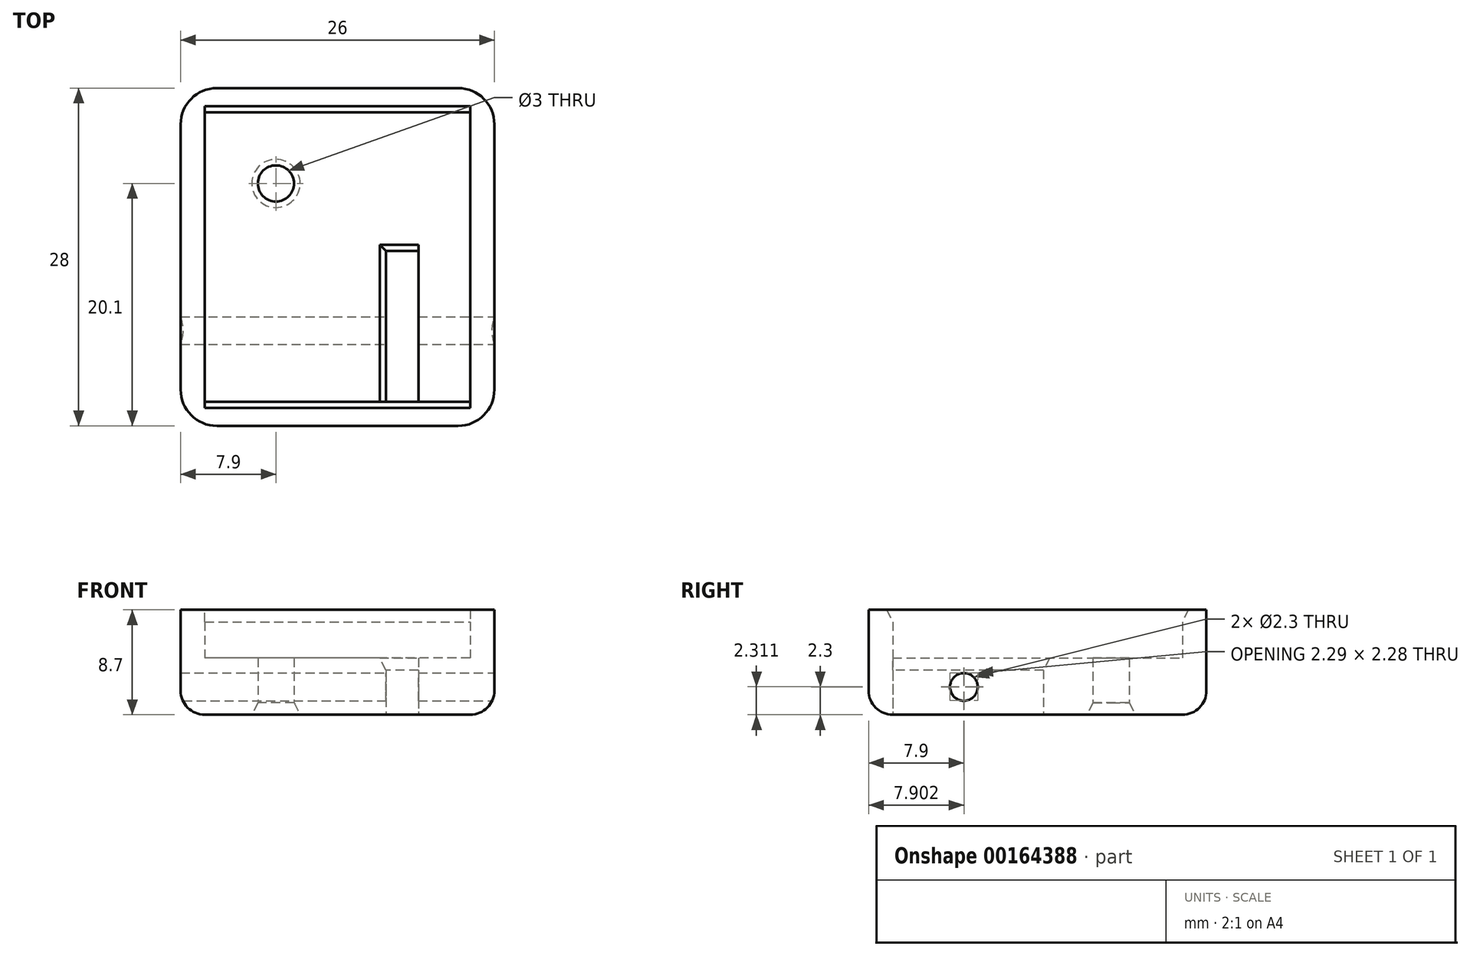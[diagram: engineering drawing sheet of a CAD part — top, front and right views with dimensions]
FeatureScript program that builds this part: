
annotation { "Feature Type Name" : "Feature", "Feature Type Description" : "" }
export const myFeature = defineFeature(function(context is Context, id is Id, definition is map)
    precondition{}
    {
        {
            var Q0;
            Q0=qCreatedBy(makeId("Top.planeOp"),FACE);
            var sketch = newSketch(context, id + "F0", { "sketchPlane" : qUnion([Q0])});
            skLineSegment(sketch, "E0.bottom", {"start": v(-11, 11.5) * mm, "end": v(11, 11.5) * mm});
            skLineSegment(sketch, "E0.top", {"start": v(-11, -12.5) * mm, "end": v(11, -12.5) * mm});
            skLineSegment(sketch, "E0.left", {"start": v(-11, 11.5) * mm, "end": v(-11, -12.5) * mm});
            skLineSegment(sketch, "E0.right", {"start": v(11, 11.5) * mm, "end": v(11, -12.5) * mm});
            skLineSegment(sketch, "E1.top", {"start": v(-11, 13.5) * mm, "end": v(11, 13.5) * mm});
            skLineSegment(sketch, "E1.left", {"start": v(-11, 11.5) * mm, "end": v(-11, 13.5) * mm});
            skLineSegment(sketch, "E1.right", {"start": v(11, 11.5) * mm, "end": v(11, 13.5) * mm});
            skLineSegment(sketch, "E2.top", {"start": v(-11, -14.5) * mm, "end": v(11, -14.5) * mm});
            skLineSegment(sketch, "E2.left", {"start": v(-11, -12.5) * mm, "end": v(-11, -14.5) * mm});
            skLineSegment(sketch, "E2.right", {"start": v(11, -12.5) * mm, "end": v(11, -14.5) * mm});
            skLineSegment(sketch, "E3.bottom", {"start": v(-11, 13.5) * mm, "end": v(-13, 13.5) * mm});
            skLineSegment(sketch, "E3.top", {"start": v(-11, -14.5) * mm, "end": v(-13, -14.5) * mm});
            skLineSegment(sketch, "E3.left", {"start": v(-11, 13.5) * mm, "end": v(-11, -14.5) * mm});
            skLineSegment(sketch, "E3.right", {"start": v(-13, 13.5) * mm, "end": v(-13, -14.5) * mm});
            skLineSegment(sketch, "E4.bottom", {"start": v(11, 13.5) * mm, "end": v(13, 13.5) * mm});
            skLineSegment(sketch, "E4.top", {"start": v(11, -14.5) * mm, "end": v(13, -14.5) * mm});
            skLineSegment(sketch, "E4.left", {"start": v(11, 13.5) * mm, "end": v(11, -14.5) * mm});
            skLineSegment(sketch, "E4.right", {"start": v(13, 13.5) * mm, "end": v(13, -14.5) * mm});
            skCircle(sketch, "E5", {"center": v(-5.1, 5.6) * mm, "radius": 1.5 * mm});
            skLineSegment(sketch, "E6.bottom", {"start": v(4, -12.5) * mm, "end": v(6.7, -12.5) * mm});
            skLineSegment(sketch, "E6.top", {"start": v(4, 0) * mm, "end": v(6.7, 0) * mm});
            skLineSegment(sketch, "E6.left", {"start": v(4, -12.5) * mm, "end": v(4, 0) * mm});
            skLineSegment(sketch, "E6.right", {"start": v(6.7, -12.5) * mm, "end": v(6.7, 0) * mm});
            skSolve(sketch);
        }
        {
            var Q0;
            Q0 = qSketchRegion(id + "F0", true);
            var Q1;
            {var subQ3=sQuery(id+"F0.wireOp",EDGE,"E0.top");Q1=makeQuery(id+"F0.imprint","IMPRINT",FACE,{"disambiguationData":[TD([[makeQuery(id+"F0.imprint","IMPRINT",EDGE,{"derivedFrom":subQ3}),1.0]])]});}
            var Q2;
            Q2=makeQuery(id+"F0.imprint","IMPRINT",FACE,{"disambiguationData":[TD([[makeQuery(id+"F0.imprint","IMPRINT",EDGE,{"derivedFrom":sQuery(id+"F0.wireOp",EDGE,"E5")}),-1.0]])]});
            var Q3;
            {var subQ0=sQuery(id+"F0.wireOp",EDGE,"E3.left");var subQ1=sQuery(id+"F0.wireOp",EDGE,"E0.bottom");var subQ2=makeQuery(id+"F0.imprint","INTERSECT",VERTEX,{"derivedFrom":[subQ1,subQ0]});Q3=makeQuery(id+"F0.imprint","IMPRINT",FACE,{"disambiguationData":[TD([[makeQuery(id+"F0.imprint","IMPRINT",EDGE,{"disambiguationData":[TD([[subQ2,-1.0]])],"derivedFrom":subQ1}),-1.0]])]});}
            extrude(context, id + "F1", {"entities" : qUnion([Q0, Q1, Q2, Q3]), "depth" : 4.7 * mm});
        }
        {
            var Q0;
            {var subQ3=sQuery(id+"F0.wireOp",EDGE,"E4.bottom");Q0=makeQuery(id+"F0.imprint","IMPRINT",FACE,{"disambiguationData":[TD([[makeQuery(id+"F0.imprint","IMPRINT",EDGE,{"derivedFrom":subQ3}),-1.0]])]});}
            var Q1;
            {var subQ0=sQuery(id+"F0.wireOp",EDGE,"E0.top");Q1=makeQuery(id+"F0.imprint","IMPRINT",FACE,{"disambiguationData":[TD([[makeQuery(id+"F0.imprint","IMPRINT",EDGE,{"derivedFrom":subQ0}),-1.0]])]});}
            var Q2;
            {var subQ3=sQuery(id+"F0.wireOp",EDGE,"E3.bottom");Q2=makeQuery(id+"F0.imprint","IMPRINT",FACE,{"disambiguationData":[TD([[makeQuery(id+"F0.imprint","IMPRINT",EDGE,{"derivedFrom":subQ3}),1.0]])]});}
            var Q3;
            {var subQ3=sQuery(id+"F0.wireOp",EDGE,"E1.top");Q3=makeQuery(id+"F0.imprint","IMPRINT",FACE,{"disambiguationData":[TD([[makeQuery(id+"F0.imprint","IMPRINT",EDGE,{"derivedFrom":subQ3}),-1.0]])]});}
            extrude(context, id + "F2", {"entities" : qUnion([Q0, Q1, Q2, Q3]), "operationType" : NewBodyOperationType.ADD, "depth" : 8.7 * mm});
        }
        {
            var Q0;
            Q0=makeQuery(id+"F1.opExtrude","CAP_FACE",FACE,{"disambiguationData":[OSD([sQuery(id+"F0.wireOp",EDGE,"E1.top"),sQuery(id+"F0.wireOp",EDGE,"E2.top"),sQuery(id+"F0.wireOp",EDGE,"E3.bottom"),sQuery(id+"F0.wireOp",EDGE,"E3.top"),sQuery(id+"F0.wireOp",EDGE,"E3.right"),sQuery(id+"F0.wireOp",EDGE,"E4.bottom"),sQuery(id+"F0.wireOp",EDGE,"E4.top"),sQuery(id+"F0.wireOp",EDGE,"E4.right")])],"isStart":false});
            var sketch = newSketch(context, id + "F3", { "sketchPlane" : qUnion([Q0])});
            skCircle(sketch, "E7", {"center": v(-5.1, 5.6) * mm, "radius": 1.5 * mm});
            skSolve(sketch);
        }
        {
            var Q0;
            Q0 = qSketchRegion(id + "F3", true);
            extrude(context, id + "F4", {"entities" : qUnion([Q0]), "operationType" : NewBodyOperationType.REMOVE, "endBound" : BoundingType.THROUGH_ALL, "oppositeDirection" : true, "depth" : 25 * mm});
        }
        {
            var Q0;
            {var subQ0=sQuery(id+"F0.wireOp",EDGE,"E4.right");Q0=makeQuery(id+"F2.boolean.opBoolean","MERGE",FACE,{"derivedFrom":[makeQuery(id+"F1.opExtrude","SWEPT_FACE",FACE,{"disambiguationData":[OSD([subQ0])]}),makeQuery(id+"F2.opExtrude","SWEPT_FACE",FACE,{"disambiguationData":[OSD([subQ0])]})]});}
            var sketch = newSketch(context, id + "F5", { "sketchPlane" : qUnion([Q0])});
            skCircle(sketch, "E8", {"center": v(-6.6, 2.3) * mm, "radius": 1.15 * mm});
            skSolve(sketch);
        }
        {
            var Q0;
            Q0=makeQuery(id+"F2.opExtrude","CAP_EDGE",EDGE,{"disambiguationData":[OSD([sQuery(id+"F0.wireOp",EDGE,"E0.bottom")])],"isStart":false});
            var Q1;
            Q1=makeQuery(id+"F2.opExtrude","CAP_EDGE",EDGE,{"disambiguationData":[OSD([sQuery(id+"F0.wireOp",EDGE,"E4.left")])],"isStart":false});
            var Q2;
            Q2=makeQuery(id+"F2.opExtrude","CAP_EDGE",EDGE,{"disambiguationData":[OSD([sQuery(id+"F0.wireOp",EDGE,"E3.left")])],"isStart":false});
            var Q3;
            Q3=makeQuery(id+"F2.opExtrude","CAP_EDGE",EDGE,{"disambiguationData":[OSD([sQuery(id+"F0.wireOp",EDGE,"E0.top"),sQuery(id+"F0.wireOp",EDGE,"E6.bottom")])],"isStart":false});
            var Q4;
            Q4=makeQuery(id+"F1.opExtrude","CAP_EDGE",EDGE,{"disambiguationData":[OSD([sQuery(id+"F0.wireOp",EDGE,"E5")])],"isStart":true});
            var Q5;
            Q5=makeQuery(id+"F1.opExtrude","CAP_EDGE",EDGE,{"disambiguationData":[OSD([sQuery(id+"F0.wireOp",EDGE,"E6.top")])],"isStart":false});
            var Q6;
            Q6=makeQuery(id+"F1.opExtrude","CAP_EDGE",EDGE,{"disambiguationData":[OSD([sQuery(id+"F0.wireOp",EDGE,"E6.left")])],"isStart":false});
            chamfer(context, id + "F6", {"entities" : qUnion([Q0, Q1, Q2, Q3, Q4, Q5, Q6]), "chamferType" : ChamferType.TWO_OFFSETS, "width1" : 0.5 * mm, "oppositeDirection" : false, "width2" : 1 * mm, "tangentPropagation" : true});
        }
        {
            var Q0;
            {var subQ0=sQuery(id+"F0.wireOp",EDGE,"E3.right");var subQ1=sQuery(id+"F0.wireOp",EDGE,"E3.top");Q0=makeQuery(id+"F2.boolean.opBoolean","MERGE",EDGE,{"derivedFrom":[makeQuery(id+"F1.opExtrude","SWEPT_EDGE",EDGE,{"disambiguationData":[OSD([subQ1,subQ0])]}),makeQuery(id+"F2.opExtrude","SWEPT_EDGE",EDGE,{"disambiguationData":[OSD([subQ1,subQ0])]})]});}
            var Q1;
            {var subQ0=sQuery(id+"F0.wireOp",EDGE,"E4.right");var subQ1=sQuery(id+"F0.wireOp",EDGE,"E4.top");Q1=makeQuery(id+"F2.boolean.opBoolean","MERGE",EDGE,{"derivedFrom":[makeQuery(id+"F1.opExtrude","SWEPT_EDGE",EDGE,{"disambiguationData":[OSD([subQ1,subQ0])]}),makeQuery(id+"F2.opExtrude","SWEPT_EDGE",EDGE,{"disambiguationData":[OSD([subQ1,subQ0])]})]});}
            var Q2;
            {var subQ0=sQuery(id+"F0.wireOp",EDGE,"E3.right");var subQ1=sQuery(id+"F0.wireOp",EDGE,"E3.bottom");Q2=makeQuery(id+"F2.boolean.opBoolean","MERGE",EDGE,{"derivedFrom":[makeQuery(id+"F1.opExtrude","SWEPT_EDGE",EDGE,{"disambiguationData":[OSD([subQ1,subQ0])]}),makeQuery(id+"F2.opExtrude","SWEPT_EDGE",EDGE,{"disambiguationData":[OSD([subQ1,subQ0])]})]});}
            var Q3;
            {var subQ0=sQuery(id+"F0.wireOp",EDGE,"E4.right");var subQ1=sQuery(id+"F0.wireOp",EDGE,"E4.bottom");Q3=makeQuery(id+"F2.boolean.opBoolean","MERGE",EDGE,{"derivedFrom":[makeQuery(id+"F1.opExtrude","SWEPT_EDGE",EDGE,{"disambiguationData":[OSD([subQ1,subQ0])]}),makeQuery(id+"F2.opExtrude","SWEPT_EDGE",EDGE,{"disambiguationData":[OSD([subQ1,subQ0])]})]});}
            fillet(context, id + "F7", {"entities" : qUnion([Q0, Q1, Q2, Q3]), "radius" : 3 * mm, "tangentPropagation" : true, "allowEdgeOverflow" : false});
        }
        {
            var Q0;
            Q0=makeQuery(id+"F1.opExtrude","CAP_EDGE",EDGE,{"disambiguationData":[OSD([sQuery(id+"F0.wireOp",EDGE,"E4.right")])],"isStart":true});
            var Q1;
            {var subQ0=sQuery(id+"F0.wireOp",EDGE,"E4.right");var subQ1=sQuery(id+"F0.wireOp",EDGE,"E4.top");Q1=makeQuery(id+"F7.opFillet","BLEND_EDGE",EDGE,{"blendedFrom":[makeQuery(id+"F2.boolean.opBoolean","MERGE",EDGE,{"derivedFrom":[makeQuery(id+"F1.opExtrude","SWEPT_EDGE",EDGE,{"disambiguationData":[OSD([subQ1,subQ0])]}),makeQuery(id+"F2.opExtrude","SWEPT_EDGE",EDGE,{"disambiguationData":[OSD([subQ1,subQ0])]})]}),makeQuery(id+"F1.opExtrude","CAP_FACE",FACE,{"disambiguationData":[OSD([sQuery(id+"F0.wireOp",EDGE,"E1.top"),sQuery(id+"F0.wireOp",EDGE,"E2.top"),sQuery(id+"F0.wireOp",EDGE,"E3.bottom"),sQuery(id+"F0.wireOp",EDGE,"E3.top"),sQuery(id+"F0.wireOp",EDGE,"E3.right"),sQuery(id+"F0.wireOp",EDGE,"E4.bottom"),subQ1,subQ0,sQuery(id+"F0.wireOp",EDGE,"E5")])],"isStart":true})],"blendedInto":[makeQuery(id+"F1.opExtrude","CAP_FACE",FACE,{"disambiguationData":[OSD([sQuery(id+"F0.wireOp",EDGE,"E1.top"),sQuery(id+"F0.wireOp",EDGE,"E2.top"),sQuery(id+"F0.wireOp",EDGE,"E3.bottom"),sQuery(id+"F0.wireOp",EDGE,"E3.top"),sQuery(id+"F0.wireOp",EDGE,"E3.right"),sQuery(id+"F0.wireOp",EDGE,"E4.bottom"),subQ1,subQ0,sQuery(id+"F0.wireOp",EDGE,"E5")])],"isStart":true})]});}
            var Q2;
            Q2=makeQuery(id+"F1.opExtrude","CAP_EDGE",EDGE,{"disambiguationData":[OSD([sQuery(id+"F0.wireOp",EDGE,"E2.top"),sQuery(id+"F0.wireOp",EDGE,"E3.top"),sQuery(id+"F0.wireOp",EDGE,"E4.top")])],"isStart":true});
            var Q3;
            {var subQ0=sQuery(id+"F0.wireOp",EDGE,"E3.right");var subQ1=sQuery(id+"F0.wireOp",EDGE,"E3.top");Q3=makeQuery(id+"F7.opFillet","BLEND_EDGE",EDGE,{"blendedFrom":[makeQuery(id+"F2.boolean.opBoolean","MERGE",EDGE,{"derivedFrom":[makeQuery(id+"F1.opExtrude","SWEPT_EDGE",EDGE,{"disambiguationData":[OSD([subQ1,subQ0])]}),makeQuery(id+"F2.opExtrude","SWEPT_EDGE",EDGE,{"disambiguationData":[OSD([subQ1,subQ0])]})]}),makeQuery(id+"F1.opExtrude","CAP_FACE",FACE,{"disambiguationData":[OSD([sQuery(id+"F0.wireOp",EDGE,"E1.top"),sQuery(id+"F0.wireOp",EDGE,"E2.top"),sQuery(id+"F0.wireOp",EDGE,"E3.bottom"),subQ1,subQ0,sQuery(id+"F0.wireOp",EDGE,"E4.bottom"),sQuery(id+"F0.wireOp",EDGE,"E4.top"),sQuery(id+"F0.wireOp",EDGE,"E4.right"),sQuery(id+"F0.wireOp",EDGE,"E5")])],"isStart":true})],"blendedInto":[makeQuery(id+"F1.opExtrude","CAP_FACE",FACE,{"disambiguationData":[OSD([sQuery(id+"F0.wireOp",EDGE,"E1.top"),sQuery(id+"F0.wireOp",EDGE,"E2.top"),sQuery(id+"F0.wireOp",EDGE,"E3.bottom"),subQ1,subQ0,sQuery(id+"F0.wireOp",EDGE,"E4.bottom"),sQuery(id+"F0.wireOp",EDGE,"E4.top"),sQuery(id+"F0.wireOp",EDGE,"E4.right"),sQuery(id+"F0.wireOp",EDGE,"E5")])],"isStart":true})]});}
            var Q4;
            {var subQ0=sQuery(id+"F0.wireOp",EDGE,"E4.right");var subQ1=sQuery(id+"F0.wireOp",EDGE,"E4.bottom");Q4=makeQuery(id+"F7.opFillet","BLEND_EDGE",EDGE,{"blendedFrom":[makeQuery(id+"F2.boolean.opBoolean","MERGE",EDGE,{"derivedFrom":[makeQuery(id+"F1.opExtrude","SWEPT_EDGE",EDGE,{"disambiguationData":[OSD([subQ1,subQ0])]}),makeQuery(id+"F2.opExtrude","SWEPT_EDGE",EDGE,{"disambiguationData":[OSD([subQ1,subQ0])]})]}),makeQuery(id+"F1.opExtrude","CAP_FACE",FACE,{"disambiguationData":[OSD([sQuery(id+"F0.wireOp",EDGE,"E1.top"),sQuery(id+"F0.wireOp",EDGE,"E2.top"),sQuery(id+"F0.wireOp",EDGE,"E3.bottom"),sQuery(id+"F0.wireOp",EDGE,"E3.top"),sQuery(id+"F0.wireOp",EDGE,"E3.right"),subQ1,sQuery(id+"F0.wireOp",EDGE,"E4.top"),subQ0,sQuery(id+"F0.wireOp",EDGE,"E5")])],"isStart":true})],"blendedInto":[makeQuery(id+"F1.opExtrude","CAP_FACE",FACE,{"disambiguationData":[OSD([sQuery(id+"F0.wireOp",EDGE,"E1.top"),sQuery(id+"F0.wireOp",EDGE,"E2.top"),sQuery(id+"F0.wireOp",EDGE,"E3.bottom"),sQuery(id+"F0.wireOp",EDGE,"E3.top"),sQuery(id+"F0.wireOp",EDGE,"E3.right"),subQ1,sQuery(id+"F0.wireOp",EDGE,"E4.top"),subQ0,sQuery(id+"F0.wireOp",EDGE,"E5")])],"isStart":true})]});}
            var Q5;
            Q5=makeQuery(id+"F1.opExtrude","CAP_EDGE",EDGE,{"disambiguationData":[OSD([sQuery(id+"F0.wireOp",EDGE,"E1.top"),sQuery(id+"F0.wireOp",EDGE,"E3.bottom"),sQuery(id+"F0.wireOp",EDGE,"E4.bottom")])],"isStart":true});
            var Q6;
            {var subQ0=sQuery(id+"F0.wireOp",EDGE,"E3.right");var subQ1=sQuery(id+"F0.wireOp",EDGE,"E3.bottom");Q6=makeQuery(id+"F7.opFillet","BLEND_EDGE",EDGE,{"blendedFrom":[makeQuery(id+"F2.boolean.opBoolean","MERGE",EDGE,{"derivedFrom":[makeQuery(id+"F1.opExtrude","SWEPT_EDGE",EDGE,{"disambiguationData":[OSD([subQ1,subQ0])]}),makeQuery(id+"F2.opExtrude","SWEPT_EDGE",EDGE,{"disambiguationData":[OSD([subQ1,subQ0])]})]}),makeQuery(id+"F1.opExtrude","CAP_FACE",FACE,{"disambiguationData":[OSD([sQuery(id+"F0.wireOp",EDGE,"E1.top"),sQuery(id+"F0.wireOp",EDGE,"E2.top"),subQ1,sQuery(id+"F0.wireOp",EDGE,"E3.top"),subQ0,sQuery(id+"F0.wireOp",EDGE,"E4.bottom"),sQuery(id+"F0.wireOp",EDGE,"E4.top"),sQuery(id+"F0.wireOp",EDGE,"E4.right"),sQuery(id+"F0.wireOp",EDGE,"E5")])],"isStart":true})],"blendedInto":[makeQuery(id+"F1.opExtrude","CAP_FACE",FACE,{"disambiguationData":[OSD([sQuery(id+"F0.wireOp",EDGE,"E1.top"),sQuery(id+"F0.wireOp",EDGE,"E2.top"),subQ1,sQuery(id+"F0.wireOp",EDGE,"E3.top"),subQ0,sQuery(id+"F0.wireOp",EDGE,"E4.bottom"),sQuery(id+"F0.wireOp",EDGE,"E4.top"),sQuery(id+"F0.wireOp",EDGE,"E4.right"),sQuery(id+"F0.wireOp",EDGE,"E5")])],"isStart":true})]});}
            var Q7;
            Q7=makeQuery(id+"F1.opExtrude","CAP_EDGE",EDGE,{"disambiguationData":[OSD([sQuery(id+"F0.wireOp",EDGE,"E3.right")])],"isStart":true});
            var Q8;
            Q8=makeQuery(id+"FJWYh7fez7YNRAC_1.opExtrude","CAP_EDGE",EDGE,{"disambiguationData":[OSD([sQuery(id+"F0.wireOp",EDGE,"lFoeRRYX-G3Lz-FDY6-PA7t-A0xL0vWlHZZd")])],"isStart":false});
            fillet(context, id + "F8", {"entities" : qUnion([Q0, Q1, Q2, Q3, Q4, Q5, Q6, Q7, Q8]), "radius" : 2 * mm, "tangentPropagation" : true, "allowEdgeOverflow" : false});
        }
        {
            var Q0;
            Q0 = qSketchRegion(id + "F5", true);
            extrude(context, id + "F9", {"entities" : qUnion([Q0]), "operationType" : NewBodyOperationType.REMOVE, "endBound" : BoundingType.THROUGH_ALL, "oppositeDirection" : true, "depth" : 25 * mm});
        }
    });
